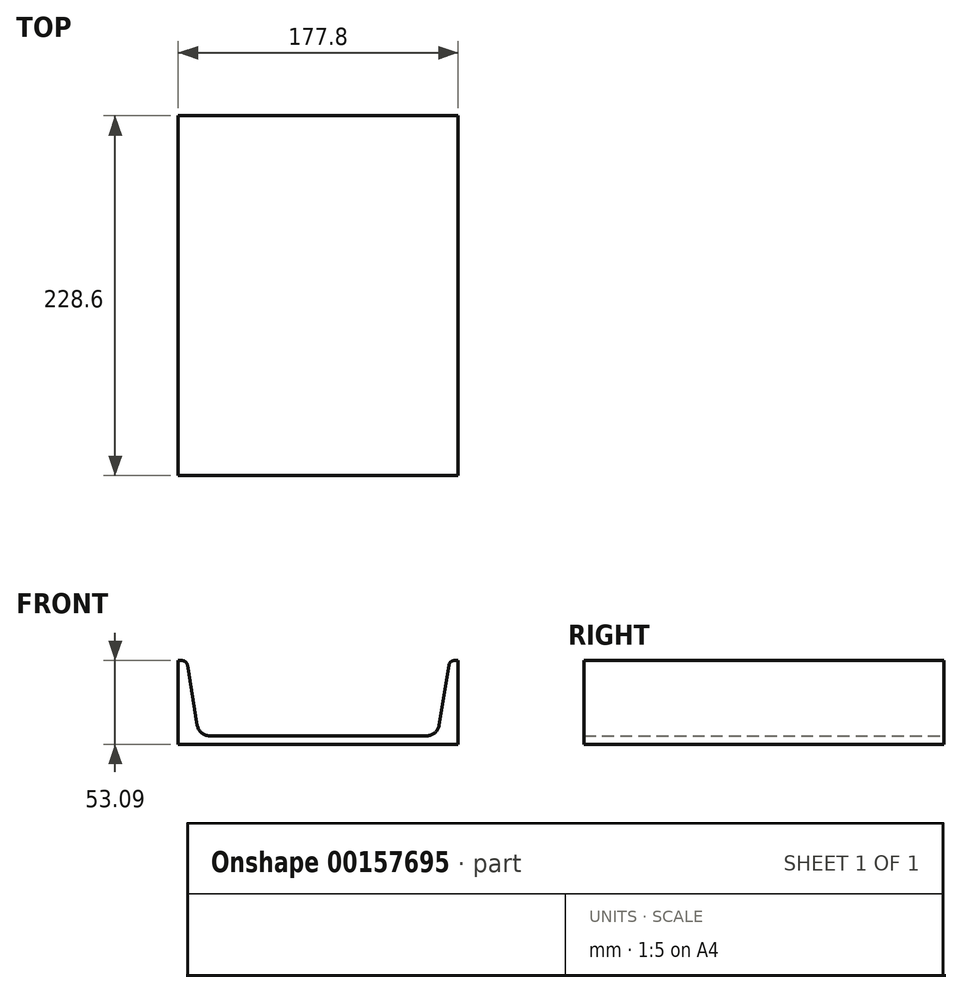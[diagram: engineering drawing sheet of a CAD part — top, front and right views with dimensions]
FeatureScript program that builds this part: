
annotation { "Feature Type Name" : "Feature", "Feature Type Description" : "" }
export const myFeature = defineFeature(function(context is Context, id is Id, definition is map)
    precondition{}
    {
        {
            var Q0;
            Q0=qCreatedBy(makeId("Front.planeOp"),FACE);
            var sketch = newSketch(context, id + "F0", { "sketchPlane" : qUnion([Q0])});
            skLineSegment(sketch, "E0", {"start": v(0, 0) * mm, "end": v(177.8, 0) * mm});
            skLineSegment(sketch, "E1", {"start": v(177.8, 0) * mm, "end": v(177.8, 53.09) * mm});
            skLineSegment(sketch, "E2", {"start": v(0, 0) * mm, "end": v(0, 53.09) * mm});
            skLineSegment(sketch, "E3", {"start": v(0, 53.09) * mm, "end": v(2.53, 53.09) * mm});
            skLineSegment(sketch, "E4", {"start": v(177.8, 53.09) * mm, "end": v(175.27, 53.09) * mm});
            skLineSegment(sketch, "E5.0", {"start": v(19.89, 5.33) * mm, "end": v(157.91, 5.33) * mm});
            skLineSegment(sketch, "E6.0", {"start": v(164.6, 5.33) * mm, "end": v(164.6, 9.04) * mm});
            skLineSegment(sketch, "E7", {"start": v(5.79, 50.32) * mm, "end": v(12.12, 11.93) * mm});
            skLineSegment(sketch, "E8", {"start": v(172.01, 50.32) * mm, "end": v(165.68, 11.93) * mm});
            skPoint(sketch, "E9.visualSharp", {"position": v(5.33, 53.09) * mm});
            skArc(sketch, "E9.filletArc", {"start": v(5.79, 50.32) * mm, "mid": v(4.67, 52.3) * mm, "end": v(2.53, 53.09) * mm});
            skPoint(sketch, "E10.visualSharp", {"position": v(13.2, 5.33) * mm});
            skArc(sketch, "E10.filletArc", {"start": v(12.12, 11.93) * mm, "mid": v(14.8, 7.2) * mm, "end": v(19.89, 5.33) * mm});
            skPoint(sketch, "E11.visualSharp", {"position": v(164.6, 5.33) * mm});
            skArc(sketch, "E11.filletArc", {"start": v(157.91, 5.33) * mm, "mid": v(163, 7.2) * mm, "end": v(165.68, 11.93) * mm});
            skPoint(sketch, "E12.visualSharp", {"position": v(172.47, 53.09) * mm});
            skArc(sketch, "E12.filletArc", {"start": v(175.27, 53.09) * mm, "mid": v(173.13, 52.3) * mm, "end": v(172.01, 50.32) * mm});
            skSolve(sketch);
        }
        {
            var Q0;
            Q0 = qSketchRegion(id + "F0", true);
            extrude(context, id + "F1", {"entities" : qUnion([Q0]), "depth" : 228.6 * mm});
        }
    });
